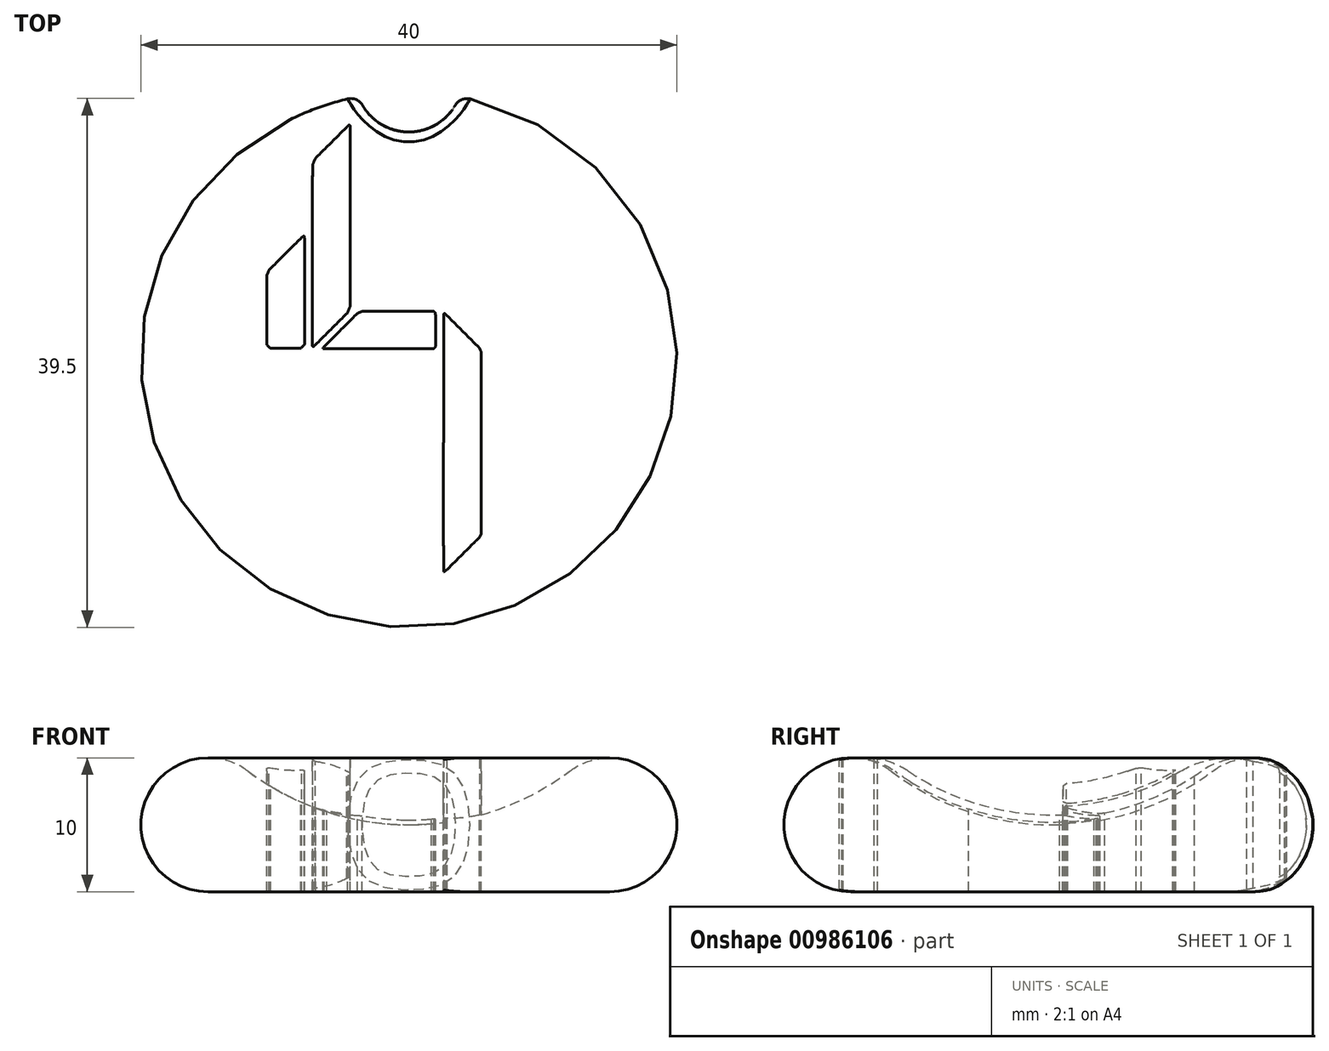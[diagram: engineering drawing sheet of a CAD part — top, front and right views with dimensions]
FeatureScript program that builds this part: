
annotation { "Feature Type Name" : "Feature", "Feature Type Description" : "" }
export const myFeature = defineFeature(function(context is Context, id is Id, definition is map)
    precondition{}
    {
        {
            var Q0;
            Q0=qCreatedBy(makeId("Front.planeOp"),FACE);
            var sketch = newSketch(context, id + "F0", { "sketchPlane" : qUnion([Q0])});
            skArc(sketch, "E0", {"start": v(-12, 9) * mm, "mid": v(-19.74, 6.58) * mm, "end": v(-15, 0) * mm});
            skArc(sketch, "E1", {"start": v(-12, 9) * mm, "mid": v(-6.32, 6.03) * mm, "end": v(0, 5) * mm});
            skLineSegment(sketch, "E2", {"start": v(-15, 0) * mm, "end": v(0, 0) * mm});
            skLineSegment(sketch, "E3", {"start": v(0, 0) * mm, "end": v(0, 5) * mm});
            skSolve(sketch);
        }
        {
            var Q0;
            Q0=makeQuery(id+"F0.imprint","IMPRINT",FACE,{"disambiguationData":[TD([[makeQuery(id+"F0.imprint","IMPRINT",EDGE,{"derivedFrom":sQuery(id+"F0.wireOp",EDGE,"E0")}),1.0]])]});
            var Q1;
            Q1=sQuery(id+"F0.wireOp",EDGE,"E3");
            revolve(context, id + "F1", {"surfaceOperationType" : NewSurfaceOperationType.NEW, "entities" : qUnion([Q0]), "axis" : qUnion([Q1]), "revolveType" : RevolveType.FULL});
        }
        {
            var Q0;
            Q0=qCreatedBy(makeId("Top.planeOp"),FACE);
            cPlane(context, id + "F2", {"entities" : qUnion([Q0]), "cplaneType" : CPlaneType.OFFSET, "offset" : 13 * mm, "width" : 152.4 * mm, "height" : 152.4 * mm});
        }
        {
            var Q0;
            Q0=qCreatedBy(id+"F2.planeOp",FACE);
            var sketch = newSketch(context, id + "F3", { "sketchPlane" : qUnion([Q0])});
            skLineSegment(sketch, "E4", {"start": v(2.6, -6.2) * mm, "end": v(2.59, -6.2) * mm});
            skLineSegment(sketch, "E5", {"start": v(2.59, -6.2) * mm, "end": v(2.59, -10.56) * mm});
            skLineSegment(sketch, "E6", {"start": v(2.59, -10.56) * mm, "end": v(2.6, -15.58) * mm});
            skLineSegment(sketch, "E7", {"start": v(2.56, -14.38) * mm, "end": v(2.59, -14.65) * mm});
            skLineSegment(sketch, "E8", {"start": v(2.62, -15.86) * mm, "end": v(2.86, -15.68) * mm});
            skLineSegment(sketch, "E9", {"start": v(2.86, -15.68) * mm, "end": v(4.92, -13.62) * mm});
            skLineSegment(sketch, "E10", {"start": v(4.92, -13.62) * mm, "end": v(5.3, -13.25) * mm});
            skLineSegment(sketch, "E11", {"start": v(5.3, -13.25) * mm, "end": v(5.4, -13) * mm});
            skLineSegment(sketch, "E12", {"start": v(5.4, -13) * mm, "end": v(5.4, -12.8) * mm});
            skLineSegment(sketch, "E13", {"start": v(5.4, -12.8) * mm, "end": v(5.4, -9.63) * mm});
            skLineSegment(sketch, "E14", {"start": v(5.4, -9.63) * mm, "end": v(5.39, 0.47) * mm});
            skLineSegment(sketch, "E15", {"start": v(5.39, 0.47) * mm, "end": v(5.39, 0.59) * mm});
            skLineSegment(sketch, "E16", {"start": v(5.39, 0.59) * mm, "end": v(5.27, 0.86) * mm});
            skLineSegment(sketch, "E17", {"start": v(5.27, 0.86) * mm, "end": v(5.2, 0.93) * mm});
            skLineSegment(sketch, "E18", {"start": v(5.2, 0.93) * mm, "end": v(2.84, 3.3) * mm});
            skLineSegment(sketch, "E19", {"start": v(2.84, 3.3) * mm, "end": v(2.7, 3.43) * mm});
            skLineSegment(sketch, "E20", {"start": v(2.7, 3.43) * mm, "end": v(2.64, 3.45) * mm});
            skLineSegment(sketch, "E21", {"start": v(2.64, 3.45) * mm, "end": v(2.6, 3.4) * mm});
            skLineSegment(sketch, "E22", {"start": v(2.6, 3.4) * mm, "end": v(2.6, 3.15) * mm});
            skLineSegment(sketch, "E23", {"start": v(2.6, 3.15) * mm, "end": v(2.6, -6.2) * mm});
            skLineSegment(sketch, "E24", {"start": v(-4.4, 10.64) * mm, "end": v(-4.4, 10.64) * mm});
            skLineSegment(sketch, "E25", {"start": v(-4.4, 10.64) * mm, "end": v(-4.4, 17.23) * mm});
            skLineSegment(sketch, "E26", {"start": v(-4.4, 17.23) * mm, "end": v(-4.4, 17.4) * mm});
            skLineSegment(sketch, "E27", {"start": v(-4.4, 17.4) * mm, "end": v(-4.4, 17.47) * mm});
            skLineSegment(sketch, "E28", {"start": v(-4.4, 17.47) * mm, "end": v(-4.42, 17.53) * mm});
            skLineSegment(sketch, "E29", {"start": v(-4.42, 17.53) * mm, "end": v(-4.5, 17.5) * mm});
            skLineSegment(sketch, "E30", {"start": v(-4.5, 17.5) * mm, "end": v(-4.64, 17.37) * mm});
            skLineSegment(sketch, "E31", {"start": v(-4.64, 17.37) * mm, "end": v(-6.99, 15.02) * mm});
            skLineSegment(sketch, "E32", {"start": v(-6.99, 15.02) * mm, "end": v(-7.19, 14.54) * mm});
            skLineSegment(sketch, "E33", {"start": v(-7.19, 14.54) * mm, "end": v(-7.2, 9.18) * mm});
            skLineSegment(sketch, "E34", {"start": v(-7.2, 9.18) * mm, "end": v(-7.2, 1.2) * mm});
            skLineSegment(sketch, "E35", {"start": v(-7.2, 1.2) * mm, "end": v(-7.2, 1.03) * mm});
            skLineSegment(sketch, "E36", {"start": v(-7.2, 1.03) * mm, "end": v(-7.17, 0.97) * mm});
            skLineSegment(sketch, "E37", {"start": v(-7.17, 0.97) * mm, "end": v(-7.1, 0.98) * mm});
            skLineSegment(sketch, "E38", {"start": v(-7.1, 0.98) * mm, "end": v(-6.95, 1.13) * mm});
            skLineSegment(sketch, "E39", {"start": v(-6.95, 1.13) * mm, "end": v(-4.58, 3.5) * mm});
            skLineSegment(sketch, "E40", {"start": v(-4.58, 3.5) * mm, "end": v(-4.4, 3.95) * mm});
            skLineSegment(sketch, "E41", {"start": v(-4.4, 3.95) * mm, "end": v(-4.4, 10.64) * mm});
            skLineSegment(sketch, "E42", {"start": v(-7.79, 5.05) * mm, "end": v(-7.79, 9.01) * mm});
            skLineSegment(sketch, "E43", {"start": v(-7.79, 9.01) * mm, "end": v(-7.82, 9.24) * mm});
            skLineSegment(sketch, "E44", {"start": v(-7.82, 9.24) * mm, "end": v(-8, 9.12) * mm});
            skLineSegment(sketch, "E45", {"start": v(-8, 9.12) * mm, "end": v(-10.44, 6.7) * mm});
            skLineSegment(sketch, "E46", {"start": v(-10.44, 6.7) * mm, "end": v(-10.6, 6.29) * mm});
            skLineSegment(sketch, "E47", {"start": v(-10.6, 6.29) * mm, "end": v(-10.6, 1.1) * mm});
            skLineSegment(sketch, "E48", {"start": v(-10.6, 1.1) * mm, "end": v(-10.33, 0.83) * mm});
            skLineSegment(sketch, "E49", {"start": v(-10.33, 0.83) * mm, "end": v(-8.07, 0.83) * mm});
            skLineSegment(sketch, "E50", {"start": v(-8.07, 0.83) * mm, "end": v(-7.79, 1.13) * mm});
            skLineSegment(sketch, "E51", {"start": v(-7.79, 1.13) * mm, "end": v(-7.79, 5.05) * mm});
            skLineSegment(sketch, "E52", {"start": v(-6.42, 0.82) * mm, "end": v(-6.13, 0.8) * mm});
            skLineSegment(sketch, "E53", {"start": v(-6.13, 0.8) * mm, "end": v(1.67, 0.8) * mm});
            skLineSegment(sketch, "E54", {"start": v(1.67, 0.8) * mm, "end": v(1.83, 0.8) * mm});
            skLineSegment(sketch, "E55", {"start": v(1.83, 0.8) * mm, "end": v(1.98, 0.94) * mm});
            skLineSegment(sketch, "E56", {"start": v(1.98, 0.94) * mm, "end": v(1.99, 1.06) * mm});
            skLineSegment(sketch, "E57", {"start": v(1.99, 1.06) * mm, "end": v(1.99, 3.34) * mm});
            skLineSegment(sketch, "E58", {"start": v(1.99, 3.34) * mm, "end": v(1.98, 3.49) * mm});
            skLineSegment(sketch, "E59", {"start": v(1.98, 3.49) * mm, "end": v(1.88, 3.6) * mm});
            skLineSegment(sketch, "E60", {"start": v(1.88, 3.6) * mm, "end": v(1.68, 3.6) * mm});
            skLineSegment(sketch, "E61", {"start": v(1.68, 3.6) * mm, "end": v(-0.17, 3.6) * mm});
            skLineSegment(sketch, "E62", {"start": v(-0.17, 3.6) * mm, "end": v(-3.49, 3.6) * mm});
            skLineSegment(sketch, "E63", {"start": v(-3.49, 3.6) * mm, "end": v(-3.83, 3.46) * mm});
            skLineSegment(sketch, "E64", {"start": v(-3.83, 3.46) * mm, "end": v(-6.33, 0.96) * mm});
            skLineSegment(sketch, "E65", {"start": v(-6.33, 0.96) * mm, "end": v(-6.4, 0.9) * mm});
            skLineSegment(sketch, "E66", {"start": v(-6.4, 0.9) * mm, "end": v(-6.42, 0.82) * mm});
            skLineSegment(sketch, "E67", {"start": v(2.6, -6.2) * mm, "end": v(2.6, 3.15) * mm});
            skLineSegment(sketch, "E68", {"start": v(2.6, 3.15) * mm, "end": v(2.6, 3.4) * mm});
            skLineSegment(sketch, "E69", {"start": v(2.6, 3.4) * mm, "end": v(2.64, 3.45) * mm});
            skLineSegment(sketch, "E70", {"start": v(2.64, 3.45) * mm, "end": v(2.7, 3.43) * mm});
            skLineSegment(sketch, "E71", {"start": v(2.7, 3.43) * mm, "end": v(2.84, 3.3) * mm});
            skLineSegment(sketch, "E72", {"start": v(2.84, 3.3) * mm, "end": v(5.2, 0.93) * mm});
            skLineSegment(sketch, "E73", {"start": v(5.2, 0.93) * mm, "end": v(5.27, 0.86) * mm});
            skLineSegment(sketch, "E74", {"start": v(5.27, 0.86) * mm, "end": v(5.39, 0.59) * mm});
            skLineSegment(sketch, "E75", {"start": v(5.39, 0.59) * mm, "end": v(5.39, 0.47) * mm});
            skLineSegment(sketch, "E76", {"start": v(5.39, 0.47) * mm, "end": v(5.4, -9.63) * mm});
            skLineSegment(sketch, "E77", {"start": v(5.4, -9.63) * mm, "end": v(5.4, -12.8) * mm});
            skLineSegment(sketch, "E78", {"start": v(5.4, -12.8) * mm, "end": v(5.4, -13) * mm});
            skLineSegment(sketch, "E79", {"start": v(5.4, -13) * mm, "end": v(5.3, -13.25) * mm});
            skLineSegment(sketch, "E80", {"start": v(5.3, -13.25) * mm, "end": v(4.92, -13.62) * mm});
            skLineSegment(sketch, "E81", {"start": v(4.92, -13.62) * mm, "end": v(2.86, -15.68) * mm});
            skLineSegment(sketch, "E82", {"start": v(2.86, -15.68) * mm, "end": v(2.62, -15.86) * mm});
            skLineSegment(sketch, "E83", {"start": v(2.62, -15.86) * mm, "end": v(2.6, -15.58) * mm});
            skLineSegment(sketch, "E84", {"start": v(2.6, -15.58) * mm, "end": v(2.59, -10.56) * mm});
            skLineSegment(sketch, "E85", {"start": v(2.59, -10.56) * mm, "end": v(2.59, -6.2) * mm});
            skLineSegment(sketch, "E86", {"start": v(2.59, -6.2) * mm, "end": v(2.6, -6.2) * mm});
            skLineSegment(sketch, "E87", {"start": v(-4.4, 10.64) * mm, "end": v(-4.4, 3.95) * mm});
            skLineSegment(sketch, "E88", {"start": v(-4.4, 3.95) * mm, "end": v(-4.58, 3.5) * mm});
            skLineSegment(sketch, "E89", {"start": v(-4.58, 3.5) * mm, "end": v(-6.95, 1.13) * mm});
            skLineSegment(sketch, "E90", {"start": v(-6.95, 1.13) * mm, "end": v(-7.1, 0.98) * mm});
            skLineSegment(sketch, "E91", {"start": v(-7.1, 0.98) * mm, "end": v(-7.17, 0.97) * mm});
            skLineSegment(sketch, "E92", {"start": v(-7.17, 0.97) * mm, "end": v(-7.2, 1.03) * mm});
            skLineSegment(sketch, "E93", {"start": v(-7.2, 1.03) * mm, "end": v(-7.2, 1.2) * mm});
            skLineSegment(sketch, "E94", {"start": v(-7.2, 1.2) * mm, "end": v(-7.2, 9.18) * mm});
            skLineSegment(sketch, "E95", {"start": v(-7.2, 9.18) * mm, "end": v(-7.19, 14.54) * mm});
            skLineSegment(sketch, "E96", {"start": v(-7.19, 14.54) * mm, "end": v(-6.99, 15.02) * mm});
            skLineSegment(sketch, "E97", {"start": v(-6.99, 15.02) * mm, "end": v(-4.64, 17.37) * mm});
            skLineSegment(sketch, "E98", {"start": v(-4.64, 17.37) * mm, "end": v(-4.5, 17.5) * mm});
            skLineSegment(sketch, "E99", {"start": v(-4.5, 17.5) * mm, "end": v(-4.42, 17.53) * mm});
            skLineSegment(sketch, "E100", {"start": v(-4.42, 17.53) * mm, "end": v(-4.4, 17.47) * mm});
            skLineSegment(sketch, "E101", {"start": v(-4.4, 17.47) * mm, "end": v(-4.4, 17.4) * mm});
            skLineSegment(sketch, "E102", {"start": v(-4.4, 17.4) * mm, "end": v(-4.4, 17.23) * mm});
            skLineSegment(sketch, "E103", {"start": v(-4.4, 17.23) * mm, "end": v(-4.4, 10.64) * mm});
            skLineSegment(sketch, "E104", {"start": v(-7.79, 5.05) * mm, "end": v(-7.79, 1.13) * mm});
            skLineSegment(sketch, "E105", {"start": v(-7.79, 1.13) * mm, "end": v(-8.07, 0.83) * mm});
            skLineSegment(sketch, "E106", {"start": v(-8.07, 0.83) * mm, "end": v(-10.33, 0.83) * mm});
            skLineSegment(sketch, "E107", {"start": v(-10.33, 0.83) * mm, "end": v(-10.6, 1.1) * mm});
            skLineSegment(sketch, "E108", {"start": v(-10.6, 1.1) * mm, "end": v(-10.6, 6.29) * mm});
            skLineSegment(sketch, "E109", {"start": v(-10.6, 6.29) * mm, "end": v(-10.44, 6.7) * mm});
            skLineSegment(sketch, "E110", {"start": v(-10.44, 6.7) * mm, "end": v(-8, 9.12) * mm});
            skLineSegment(sketch, "E111", {"start": v(-8, 9.12) * mm, "end": v(-7.82, 9.24) * mm});
            skLineSegment(sketch, "E112", {"start": v(-7.82, 9.24) * mm, "end": v(-7.79, 9.01) * mm});
            skLineSegment(sketch, "E113", {"start": v(-7.79, 9.01) * mm, "end": v(-7.79, 5.05) * mm});
            skLineSegment(sketch, "E114", {"start": v(-6.42, 0.82) * mm, "end": v(-6.4, 0.9) * mm});
            skLineSegment(sketch, "E115", {"start": v(-6.4, 0.9) * mm, "end": v(-6.33, 0.96) * mm});
            skLineSegment(sketch, "E116", {"start": v(-6.33, 0.96) * mm, "end": v(-3.83, 3.46) * mm});
            skLineSegment(sketch, "E117", {"start": v(-3.83, 3.46) * mm, "end": v(-3.49, 3.6) * mm});
            skLineSegment(sketch, "E118", {"start": v(-3.49, 3.6) * mm, "end": v(-0.17, 3.6) * mm});
            skLineSegment(sketch, "E119", {"start": v(-0.17, 3.6) * mm, "end": v(1.68, 3.6) * mm});
            skLineSegment(sketch, "E120", {"start": v(1.68, 3.6) * mm, "end": v(1.88, 3.6) * mm});
            skLineSegment(sketch, "E121", {"start": v(1.88, 3.6) * mm, "end": v(1.98, 3.49) * mm});
            skLineSegment(sketch, "E122", {"start": v(1.98, 3.49) * mm, "end": v(1.99, 3.34) * mm});
            skLineSegment(sketch, "E123", {"start": v(1.99, 3.34) * mm, "end": v(1.99, 1.06) * mm});
            skLineSegment(sketch, "E124", {"start": v(1.99, 1.06) * mm, "end": v(1.98, 0.94) * mm});
            skLineSegment(sketch, "E125", {"start": v(1.98, 0.94) * mm, "end": v(1.83, 0.8) * mm});
            skLineSegment(sketch, "E126", {"start": v(1.83, 0.8) * mm, "end": v(1.67, 0.8) * mm});
            skLineSegment(sketch, "E127", {"start": v(1.67, 0.8) * mm, "end": v(-6.13, 0.8) * mm});
            skLineSegment(sketch, "E128", {"start": v(-6.13, 0.8) * mm, "end": v(-6.42, 0.82) * mm});
            skPoint(sketch, "E129", {"position": v(3.89, -14.65) * mm});
            skSolve(sketch);
        }
        {
            var Q0;
            Q0 = qSketchRegion(id + "F3", true);
            extrude(context, id + "F4", {"entities" : qUnion([Q0]), "operationType" : NewBodyOperationType.REMOVE, "oppositeDirection" : true, "depth" : 25.4 * mm, "offsetDistance" : 25.4 * mm});
        }
        {
            var Q0;
            Q0=qCreatedBy(makeId("Top.planeOp"),FACE);
            var sketch = newSketch(context, id + "F5", { "sketchPlane" : qUnion([Q0])});
            skCircle(sketch, "E130", {"center": v(0, 21) * mm, "radius": 4 * mm});
            skSolve(sketch);
        }
        {
            var Q0;
            Q0 = qSketchRegion(id + "F5", true);
            extrude(context, id + "F6", {"entities" : qUnion([Q0]), "operationType" : NewBodyOperationType.REMOVE, "depth" : 25.4 * mm, "offsetDistance" : 25.4 * mm});
        }
        {
            var Q0;
            Q0=makeQuery(id+"F6.boolean.opBoolean","INTERSECT",EDGE,{"derivedFrom":[makeQuery(id+"F1.opRevolve","SWEPT_FACE",FACE,{"disambiguationData":[OSD([sQuery(id+"F0.wireOp",EDGE,"E0")])]}),makeQuery(id+"F6.opExtrude","SWEPT_FACE",FACE,{"disambiguationData":[OSD([sQuery(id+"F5.wireOp",EDGE,"E130")])]})]});
            fillet(context, id + "F7", {"entities" : qUnion([Q0]), "radius" : 1 * mm, "tangentPropagation" : true, "allowEdgeOverflow" : false});
        }
    });
